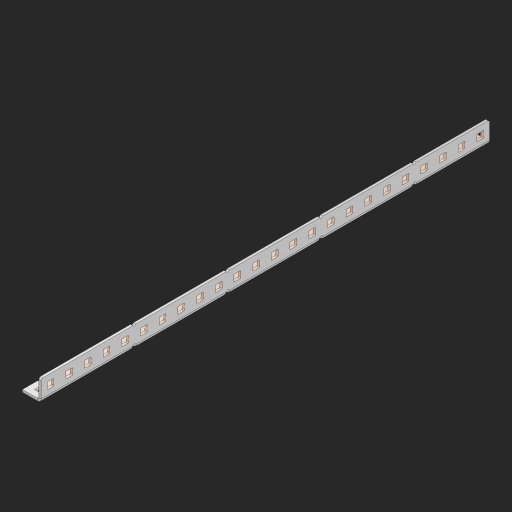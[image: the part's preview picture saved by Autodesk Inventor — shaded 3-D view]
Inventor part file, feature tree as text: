
AUTODESK INVENTOR PART (.ipt)
format: ipt  version: 2023 (Build 270158000, 158)  size: 1,091,584 bytes
history: native  units: in
note: dims shown in document units (in); Inventor stores cm internally (conversion verified against a paired STEP export)
features: other x220, extrude x70, sheet_metal_op x11, sketch x10, pattern_linear x2, mirror x1, chamfer x1
ambient origin geometry x8: Origin, YZ Plane, XZ Plane, XY Plane, X Axis, Y Axis, Z Axis, Center Point
bodies: Solid1 (feature_tree), Body (feature_tree)
feature tree (315):
  other  "Alu Half C 1x2x1x24"
  other  "Table"
  other  "Alu C 1x2x1x35"
  other  "Alu C 1x2x1x34"
  other  "Alu C 1x2x1x33"
  other  "Alu C 1x2x1x32"
  other  "Alu C 1x2x1x31"
  other  "Alu C 1x2x1x30"
  other  "Alu C 1x2x1x29"
  other  "Alu C 1x2x1x28"
  other  "Alu C 1x2x1x27"
  other  "Alu C 1x2x1x26"
  other  "Alu C 1x2x1x25"
  other  "Alu C 1x2x1x24"
  other  "Alu C 1x2x1x23"
  other  "Alu C 1x2x1x22"
  other  "Alu C 1x2x1x21"
  other  "Alu C 1x2x1x20"
  other  "Alu C 1x2x1x19"
  other  "Alu C 1x2x1x18"
  other  "Alu C 1x2x1x17"
  other  "Alu C 1x2x1x16"
  other  "Alu C 1x2x1x15"
  other  "Alu C 1x2x1x14"
  other  "Alu C 1x2x1x13"
  other  "Alu C 1x2x1x12"
  other  "Alu C 1x2x1x11"
  other  "Alu C 1x2x1x10"
  other  "Alu C 1x2x1x9"
  other  "Alu C 1x2x1x8"
  other  "Alu C 1x2x1x7"
  other  "Alu C 1x2x1x6"
  other  "Alu C 1x2x1x5"
  other  "Alu C 1x2x1x4"
  other  "Alu C 1x2x1x3"
  other  "Alu C 1x2x1x2"
  other  "Alu C 1x2x1x1"
  other  "Steel C 1x2x1x35"
  other  "Steel C 1x2x1x34"
  other  "Steel C 1x2x1x33"
  other  "Steel C 1x2x1x32"
  other  "Steel C 1x2x1x31"
  other  "Steel C 1x2x1x30"
  other  "Steel C 1x2x1x29"
  other  "Steel C 1x2x1x28"
  other  "Steel C 1x2x1x27"
  other  "Steel C 1x2x1x26"
  other  "Steel C 1x2x1x25"
  other  "Steel C 1x2x1x24"
  other  "Steel C 1x2x1x23"
  other  "Steel C 1x2x1x22"
  other  "Steel C 1x2x1x21"
  other  "Steel C 1x2x1x20"
  other  "Steel C 1x2x1x19"
  other  "Steel C 1x2x1x18"
  other  "Steel C 1x2x1x17"
  other  "Steel C 1x2x1x16"
  other  "Steel C 1x2x1x15"
  other  "Steel C 1x2x1x14"
  other  "Steel C 1x2x1x13"
  other  "Steel C 1x2x1x12"
  other  "Steel C 1x2x1x11"
  other  "Steel C 1x2x1x10"
  other  "Steel C 1x2x1x9"
  other  "Steel C 1x2x1x8"
  other  "Steel C 1x2x1x7"
  other  "Steel C 1x2x1x6"
  other  "Steel C 1x2x1x5"
  other  "Steel C 1x2x1x4"
  other  "Steel C 1x2x1x3"
  other  "Steel C 1x2x1x2"
  other  "Steel C 1x2x1x1"
  other  "Alu Half C 1x2x1x35"
  other  "Alu Half C 1x2x1x34"
  other  "Alu Half C 1x2x1x33"
  other  "Alu Half C 1x2x1x32"
  other  "Alu Half C 1x2x1x31"
  other  "Alu Half C 1x2x1x30"
  other  "Alu Half C 1x2x1x29"
  other  "Alu Half C 1x2x1x28"
  other  "Alu Half C 1x2x1x27"
  other  "Alu Half C 1x2x1x26"
  other  "Alu Half C 1x2x1x25"
  other  "Alu Half C 1x2x1x23"
  other  "Alu Half C 1x2x1x22"
  other  "Alu Half C 1x2x1x21"
  other  "Alu Half C 1x2x1x20"
  other  "Alu Half C 1x2x1x19"
  other  "Alu Half C 1x2x1x18"
  other  "Alu Half C 1x2x1x17"
  other  "Alu Half C 1x2x1x16"
  other  "Alu Half C 1x2x1x15"
  other  "Alu Half C 1x2x1x14"
  other  "Alu Half C 1x2x1x13"
  other  "Alu Half C 1x2x1x12"
  other  "Alu Half C 1x2x1x11"
  other  "Alu Half C 1x2x1x10"
  other  "Alu Half C 1x2x1x9"
  other  "Alu Half C 1x2x1x8"
  other  "Alu Half C 1x2x1x7"
  other  "Alu Half C 1x2x1x6"
  other  "Alu Half C 1x2x1x5"
  other  "Alu Half C 1x2x1x4"
  other  "Alu Half C 1x2x1x3"
  other  "Alu Half C 1x2x1x2"
  other  "Alu Half C 1x2x1x1"
  other  "Steel Half C 1x2x1x35"
  other  "Steel Half C 1x2x1x34"
  other  "Steel Half C 1x2x1x33"
  other  "Steel Half C 1x2x1x32"
  other  "Steel Half C 1x2x1x31"
  other  "Steel Half C 1x2x1x30"
  other  "Steel Half C 1x2x1x29"
  other  "Steel Half C 1x2x1x28"
  other  "Steel Half C 1x2x1x27"
  other  "Steel Half C 1x2x1x26"
  other  "Steel Half C 1x2x1x25"
  other  "Steel Half C 1x2x1x24"
  other  "Steel Half C 1x2x1x23"
  other  "Steel Half C 1x2x1x22"
  other  "Steel Half C 1x2x1x21"
  other  "Steel Half C 1x2x1x20"
  other  "Steel Half C 1x2x1x19"
  other  "Steel Half C 1x2x1x18"
  other  "Steel Half C 1x2x1x17"
  other  "Steel Half C 1x2x1x16"
  other  "Steel Half C 1x2x1x15"
  other  "Steel Half C 1x2x1x14"
  other  "Steel Half C 1x2x1x13"
  other  "Steel Half C 1x2x1x12"
  other  "Steel Half C 1x2x1x11"
  other  "Steel Half C 1x2x1x10"
  other  "Steel Half C 1x2x1x9"
  other  "Steel Half C 1x2x1x8"
  other  "Steel Half C 1x2x1x7"
  other  "Steel Half C 1x2x1x6"
  other  "Steel Half C 1x2x1x5"
  other  "Steel Half C 1x2x1x4"
  other  "Steel Half C 1x2x1x3"
  other  "Steel Half C 1x2x1x2"
  other  "Steel Half C 1x2x1x1"
  sheet_metal_op  "Flanges"
  other  "Flange Pattern Plane"
  other  "Flange Pattern Sketch"
  sheet_metal_op  "Flange Pattern"
  sheet_metal_op  "Body Pattern"
  pattern_linear  "Center Pattern"  Spacing1=0.0625in  [1 undecoded]
  other  "Arc Length"
  mirror  "Notch Mirror"
  pattern_linear  "Notch Pattern"  Spacing1=0.182in  [1 undecoded]
  chamfer  "End Chamfer"
  extrude  "Half Cut"  Depth=0.02in
  sketch  "Sketch1"  dims[d0=1.0in]
  other  "Plate1"
  sketch  "Sketch2"  dims[d1=12.0in]
  other  "Plate2"
  sheet_metal_op  "Bend1"
  sheet_metal_op  "Corner1"
  sketch  "Sketch3"  dims[d2=0.0625in]
  sketch  "Sketch7"  dims[d3=0.0625in]
  other  "Srf1"
  other  "Srf2"
  sketch  "Sketch8"  dims[d4=0.0312in]
  sketch  "Sketch9"  dims[d5=0.125in]
  other  "Srf91"
  sheet_metal_op  "Body Pattern Sketch"
  other  "Srf92"
  sketch  "Sketch13"  dims[d6=0.0625in]
  sketch  "Sketch14"  dims[d7=0.5in d8=90.0deg d9=0.0312in]
  sketch  "Sketch15"  dims[d10=0.25in]
  sketch  "Sketch16"  dims[d11=0.0625in d12=0.0625in d16=0.182in d17=0.02in d18=0.0625in d19=0.0in d20=0.25in d21=0.25in d38=9.4488in d40=0.5in d41=0.3937in d43=1.0in d46=0.172in d47=1.0in d48=0.0in d49=0.182in d50=0.02in d51=0.25in d52=0.25in d53=0.0625in d54=0.0in d55=0.172in d56=1.0in d57=0.0in d58=0.25in d60=9.4488in d62=0.5in d63=0.3937in d65=0.5in d85=0.1473in d86=0.1782in d88=0.04in d89=0.0625in d90=0.0in d91=0.04in d92=0.0491in d95=2.5in d96=0.04in d97=0.25in d98=45.0deg d99=0.25in d100=0.5in d101=0.0in d102=2.497in d106=0.182in d107=0.02in d108=0.5in d109=0.5in d110=0.0625in d111=0.0in d112=0.172in d113=0.5in d114=0.0in d117=0.5in d118=0.5in d119=0.5in]
  other  "Srf786"
  other  "Srf823"
  other  "Srf824"
  other  "Srf825"
  other  "Srf826"
  other  "Srf827"
  other  "Srf828"
  other  "Srf829"
  other  "Srf856"
  other  "Srf857"
  other  "Srf858"
  other  "Srf859"
  other  "Srf860"
  other  "Srf861"
  other  "Srf862"
  other  "Srf889"
  other  "Srf890"
  other  "Srf891"
  other  "Srf892"
  other  "Srf893"
  other  "Srf894"
  other  "Srf895"
  other  "Srf896"
  other  "Srf922"
  other  "Srf923"
  other  "Srf924"
  other  "Srf925"
  other  "Srf926"
  other  "Srf959"
  other  "Srf960"
  other  "Srf961"
  other  "Srf962"
  other  "Srf963"
  other  "Srf996"
  other  "Srf997"
  other  "Srf998"
  other  "Srf999"
  other  "Srf1000"
  other  "Srf1143"
  other  "Srf1144"
  other  "Srf1145"
  other  "Srf1146"
  other  "Srf1147"
  other  "Srf1148"
  other  "Srf1149"
  other  "Srf1150"
  other  "Srf1151"
  other  "Srf1152"
  other  "Srf1199"
  other  "Srf1200"
  other  "Srf1201"
  other  "Srf1202"
  other  "Srf1203"
  other  "Srf1204"
  other  "Srf1205"
  other  "Srf1206"
  other  "Srf1207"
  other  "Srf1208"
  other  "Srf1255"
  other  "Srf1256"
  other  "Srf1257"
  other  "Srf1258"
  other  "Srf1259"
  other  "Srf1260"
  other  "Srf1261"
  other  "Srf1262"
  other  "Srf1263"
  other  "Srf1264"
  sheet_metal_op  "Flange Stamp"
  sheet_metal_op  "Flange Circle"
  sheet_metal_op  "Body Stamp"
  sheet_metal_op  "Body Circle"
  other  "Center Stamp"
  other  "Center Circle"
  sheet_metal_op  "Notch"
  extrude  "ExtrusionSrf2"  Depth=0.0625in
  extrude  "ExtrusionSrf92"  TaperAngle=0.0deg  [1 undecoded]
  extrude  "ExtrusionSrf823"  Depth=0.25in
  extrude  "ExtrusionSrf824"  Depth=0.25in
  extrude  "ExtrusionSrf825"  Depth=0.5in
  extrude  "ExtrusionSrf826"  Depth=0.5in
  extrude  "ExtrusionSrf827"  Depth=1.0in TaperAngle=0.0deg
  extrude  "ExtrusionSrf828"  Depth=0.182in
  extrude  "ExtrusionSrf829"  Depth=0.02in
  extrude  "ExtrusionSrf856"  Depth=0.25in
  extrude  "ExtrusionSrf857"  Depth=0.25in
  extrude  "ExtrusionSrf858"  Depth=0.0625in
  extrude  "ExtrusionSrf859"  TaperAngle=0.0deg  [1 undecoded]
  extrude  "ExtrusionSrf860"  Depth=0.5in
  extrude  "ExtrusionSrf861"  Depth=1.0in TaperAngle=0.0deg
  extrude  "ExtrusionSrf862"  Depth=0.25in
  extrude  "ExtrusionSrf889"  Depth=0.5in
  extrude  "ExtrusionSrf890"  Depth=0.5in
  extrude  "ExtrusionSrf891"  Depth=0.5in
  extrude  "ExtrusionSrf892"  Depth=0.5in
  extrude  "ExtrusionSrf893"  Depth=0.5in
  extrude  "ExtrusionSrf894"  Depth=0.0625in
  extrude  "ExtrusionSrf895"  TaperAngle=0.0deg  [1 undecoded]
  extrude  "ExtrusionSrf896"  Depth=0.5in
  extrude  "ExtrusionSrf922"  Depth=0.5in
  extrude  "ExtrusionSrf923"  Depth=2.5in
  extrude  "ExtrusionSrf924"  Depth=0.25in TaperAngle=45.0deg
  extrude  "ExtrusionSrf925"  Depth=0.25in
  extrude  "ExtrusionSrf926"  Depth=0.5in TaperAngle=0.0deg
  extrude  "ExtrusionSrf959"  Depth=0.5in
  extrude  "ExtrusionSrf960"  Depth=0.182in
  extrude  "ExtrusionSrf961"  Depth=0.02in
  extrude  "ExtrusionSrf962"  Depth=0.5in
  extrude  "ExtrusionSrf963"  Depth=0.5in
  extrude  "ExtrusionSrf996"  Depth=0.0625in
  extrude  "ExtrusionSrf997"  TaperAngle=0.0deg  [1 undecoded]
  extrude  "ExtrusionSrf998"  Depth=0.5in
  extrude  "ExtrusionSrf999"  Depth=0.5in TaperAngle=0.0deg
  extrude  "ExtrusionSrf1000"  Depth=0.5in
  extrude  "ExtrusionSrf1143"  Depth=0.5in
  extrude  "ExtrusionSrf1144"  Depth=0.5in
  extrude  "ExtrusionSrf1145"  [1 undecoded]
  extrude  "ExtrusionSrf1146"  [1 undecoded]
  extrude  "ExtrusionSrf1147"  [1 undecoded]
  extrude  "ExtrusionSrf1148"  [1 undecoded]
  extrude  "ExtrusionSrf1149"  [1 undecoded]
  extrude  "ExtrusionSrf1150"  [1 undecoded]
  extrude  "ExtrusionSrf1151"  [1 undecoded]
  extrude  "ExtrusionSrf1152"  [1 undecoded]
  extrude  "ExtrusionSrf1199"  [1 undecoded]
  extrude  "ExtrusionSrf1200"  [1 undecoded]
  extrude  "ExtrusionSrf1201"  [1 undecoded]
  extrude  "ExtrusionSrf1202"  [1 undecoded]
  extrude  "ExtrusionSrf1203"  [1 undecoded]
  extrude  "ExtrusionSrf1204"  [1 undecoded]
  extrude  "ExtrusionSrf1205"  [1 undecoded]
  extrude  "ExtrusionSrf1206"  [1 undecoded]
  extrude  "ExtrusionSrf1207"  [1 undecoded]
  extrude  "ExtrusionSrf1208"  [1 undecoded]
  extrude  "ExtrusionSrf1255"  [1 undecoded]
  extrude  "ExtrusionSrf1256"  [1 undecoded]
  extrude  "ExtrusionSrf1257"  [1 undecoded]
  extrude  "ExtrusionSrf1258"  [1 undecoded]
  extrude  "ExtrusionSrf1259"  [1 undecoded]
  extrude  "ExtrusionSrf1260"  [1 undecoded]
  extrude  "ExtrusionSrf1261"  [1 undecoded]
  extrude  "ExtrusionSrf1262"  [1 undecoded]
  extrude  "ExtrusionSrf1263"  [1 undecoded]
  extrude  "ExtrusionSrf1264"  [1 undecoded]
note: 34 required parameter values undecoded (feature->parameter linkage not recoverable at this tier; creation-order binding heuristic only, values carry confidence <= 0.55)
